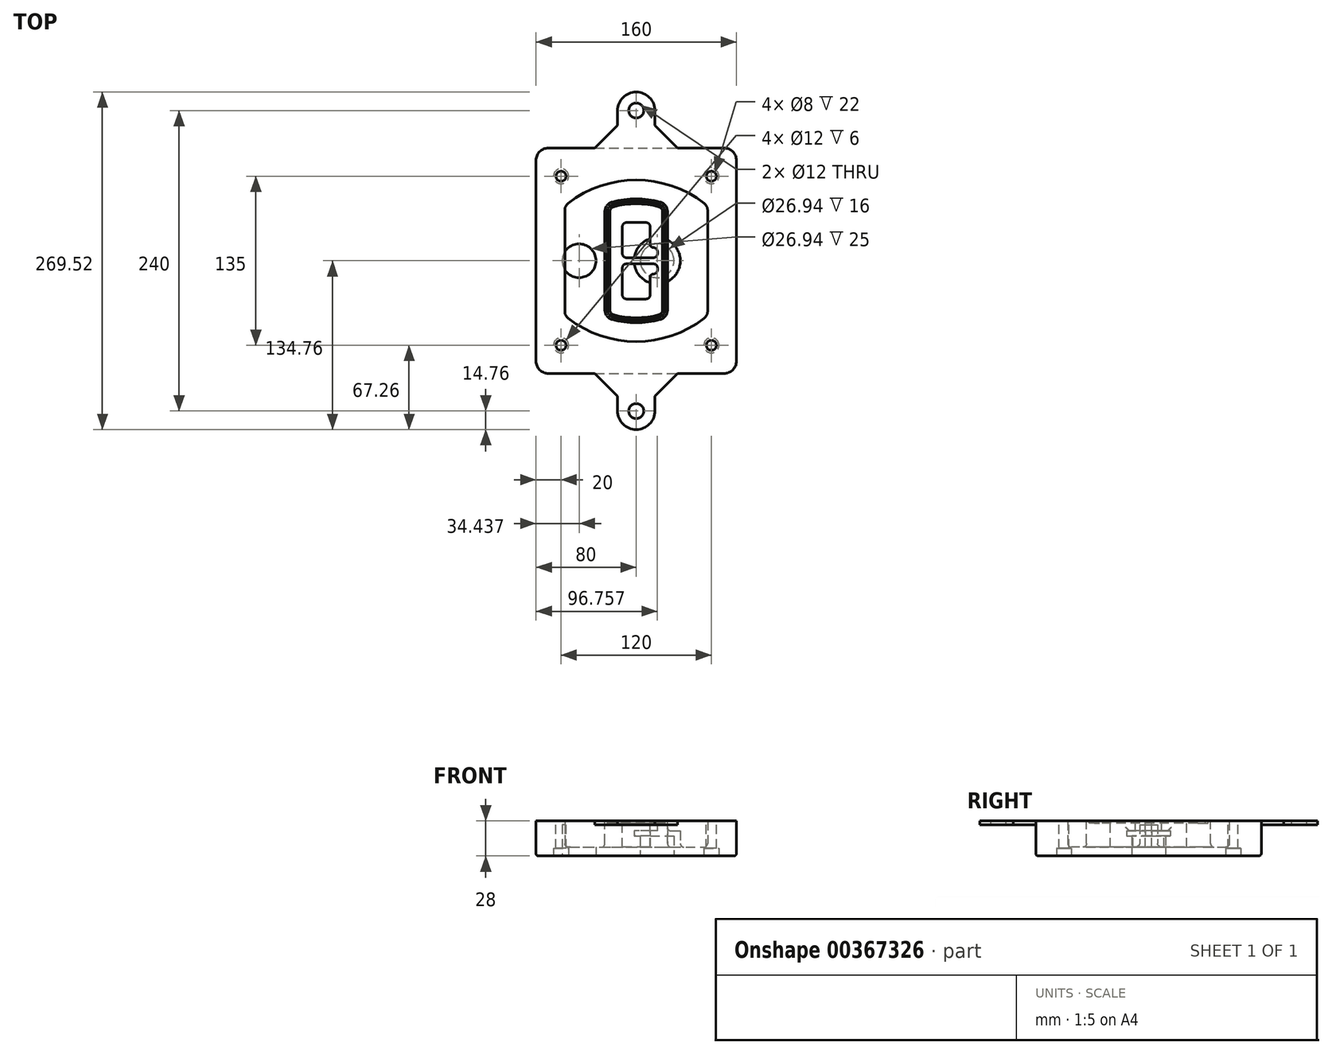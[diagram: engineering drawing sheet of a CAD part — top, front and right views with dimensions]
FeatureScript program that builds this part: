
annotation { "Feature Type Name" : "Feature", "Feature Type Description" : "" }
export const myFeature = defineFeature(function(context is Context, id is Id, definition is map)
    precondition{}
    {
        {
            var Q0;
            Q0=qCreatedBy(makeId("Top.planeOp"),FACE);
            var sketch = newSketch(context, id + "F0", { "sketchPlane" : qUnion([Q0])});
            skPoint(sketch, "E0.rect.middle", {"position": v(0, 0) * mm});
            skLineSegment(sketch, "E1.bottom", {"start": v(-70, -90) * mm, "end": v(70, -90) * mm});
            skLineSegment(sketch, "E1.top", {"start": v(-70, 90) * mm, "end": v(70, 90) * mm});
            skLineSegment(sketch, "E1.left", {"start": v(-80, -80) * mm, "end": v(-80, 80) * mm});
            skLineSegment(sketch, "E1.right", {"start": v(80, -80) * mm, "end": v(80, 80) * mm});
            skLineSegment(sketch, "E2", {"start": v(-80, 90) * mm, "end": v(80, -90) * mm, "construction": true});
            skLineSegment(sketch, "E3", {"start": v(80, 90) * mm, "end": v(-80, -90) * mm, "construction": true});
            skCircle(sketch, "E4", {"center": v(-60, 67.5) * mm, "radius": 4 * mm});
            skCircle(sketch, "E5", {"center": v(60, 67.5) * mm, "radius": 4 * mm});
            skCircle(sketch, "E6", {"center": v(60, -67.5) * mm, "radius": 4 * mm});
            skCircle(sketch, "E7", {"center": v(-60, -67.5) * mm, "radius": 4 * mm});
            skLineSegment(sketch, "E8", {"start": v(-60, 67.5) * mm, "end": v(60, 67.5) * mm, "construction": true});
            skLineSegment(sketch, "E9", {"start": v(60, 67.5) * mm, "end": v(60, -67.5) * mm, "construction": true});
            skLineSegment(sketch, "E10", {"start": v(60, -67.5) * mm, "end": v(-60, -67.5) * mm, "construction": true});
            skLineSegment(sketch, "E11", {"start": v(-60, -67.5) * mm, "end": v(-60, 67.5) * mm, "construction": true});
            skLineSegment(sketch, "E12", {"start": v(-60, 40.3) * mm, "end": v(-60, -40.3) * mm});
            skLineSegment(sketch, "E13", {"start": v(60, 40.3) * mm, "end": v(60, -40.3) * mm});
            skArc(sketch, "E14", {"start": v(56.15, 48.18) * mm, "mid": v(0, 67.5) * mm, "end": v(-56.15, 48.18) * mm});
            skArc(sketch, "E15", {"start": v(-56.15, -48.18) * mm, "mid": v(0, -67.5) * mm, "end": v(56.15, -48.18) * mm});
            skLineSegment(sketch, "E16", {"start": v(-60, 0) * mm, "end": v(60, 0) * mm, "construction": true});
            skPoint(sketch, "E17.visualSharp", {"position": v(-60, -45) * mm});
            skArc(sketch, "E17.filletArc", {"start": v(-60, -40.3) * mm, "mid": v(-58.99, -44.68) * mm, "end": v(-56.15, -48.18) * mm});
            skPoint(sketch, "E18.visualSharp", {"position": v(-60, 45) * mm});
            skArc(sketch, "E18.filletArc", {"start": v(-56.15, 48.18) * mm, "mid": v(-58.99, 44.68) * mm, "end": v(-60, 40.3) * mm});
            skPoint(sketch, "E19.visualSharp", {"position": v(60, 45) * mm});
            skArc(sketch, "E19.filletArc", {"start": v(60, 40.3) * mm, "mid": v(58.99, 44.68) * mm, "end": v(56.15, 48.18) * mm});
            skPoint(sketch, "E20.visualSharp", {"position": v(60, -45) * mm});
            skArc(sketch, "E20.filletArc", {"start": v(56.15, -48.18) * mm, "mid": v(58.99, -44.68) * mm, "end": v(60, -40.3) * mm});
            skPoint(sketch, "E21.visualSharp", {"position": v(-80, 90) * mm});
            skArc(sketch, "E21.filletArc", {"start": v(-70, 90) * mm, "mid": v(-77.07, 87.07) * mm, "end": v(-80, 80) * mm});
            skPoint(sketch, "E22.visualSharp", {"position": v(80, 90) * mm});
            skArc(sketch, "E22.filletArc", {"start": v(80, 80) * mm, "mid": v(77.07, 87.07) * mm, "end": v(70, 90) * mm});
            skPoint(sketch, "E23.visualSharp", {"position": v(80, -90) * mm});
            skArc(sketch, "E23.filletArc", {"start": v(70, -90) * mm, "mid": v(77.07, -87.07) * mm, "end": v(80, -80) * mm});
            skPoint(sketch, "E24.visualSharp", {"position": v(-80, -90) * mm});
            skArc(sketch, "E24.filletArc", {"start": v(-80, -80) * mm, "mid": v(-77.07, -87.07) * mm, "end": v(-70, -90) * mm});
            skArc(sketch, "E25.0", {"start": v(57, 40.3) * mm, "mid": v(56.3, 43.36) * mm, "end": v(54.3, 45.81) * mm});
            skLineSegment(sketch, "E25.1", {"start": v(57, 40.3) * mm, "end": v(57, -40.3) * mm});
            skArc(sketch, "E25.2", {"start": v(54.3, -45.81) * mm, "mid": v(56.3, -43.36) * mm, "end": v(57, -40.3) * mm});
            skArc(sketch, "E25.3", {"start": v(-54.3, -45.81) * mm, "mid": v(0, -64.5) * mm, "end": v(54.3, -45.81) * mm});
            skArc(sketch, "E25.4", {"start": v(-57, -40.3) * mm, "mid": v(-56.3, -43.36) * mm, "end": v(-54.3, -45.81) * mm});
            skArc(sketch, "E25.5", {"start": v(54.3, 45.81) * mm, "mid": v(0, 64.5) * mm, "end": v(-54.3, 45.81) * mm});
            skLineSegment(sketch, "E25.6", {"start": v(-57, 40.3) * mm, "end": v(-57, -40.3) * mm});
            skArc(sketch, "E25.7", {"start": v(-54.3, 45.81) * mm, "mid": v(-56.3, 43.36) * mm, "end": v(-57, 40.3) * mm});
            skArc(sketch, "E26.0", {"start": v(-58.62, 51.33) * mm, "mid": v(-62.58, 46.43) * mm, "end": v(-64, 40.3) * mm});
            skArc(sketch, "E26.1", {"start": v(58.62, 51.33) * mm, "mid": v(0, 71.5) * mm, "end": v(-58.62, 51.33) * mm});
            skArc(sketch, "E26.2", {"start": v(64, 40.3) * mm, "mid": v(62.58, 46.43) * mm, "end": v(58.62, 51.33) * mm});
            skLineSegment(sketch, "E26.3", {"start": v(64, 40.3) * mm, "end": v(64, -40.3) * mm});
            skArc(sketch, "E26.4", {"start": v(58.62, -51.33) * mm, "mid": v(62.58, -46.43) * mm, "end": v(64, -40.3) * mm});
            skLineSegment(sketch, "E26.5", {"start": v(-64, 40.3) * mm, "end": v(-64, -40.3) * mm});
            skArc(sketch, "E26.6", {"start": v(-58.62, -51.33) * mm, "mid": v(0, -71.5) * mm, "end": v(58.62, -51.33) * mm});
            skArc(sketch, "E26.7", {"start": v(-64, -40.3) * mm, "mid": v(-62.58, -46.43) * mm, "end": v(-58.62, -51.33) * mm});
            skSolve(sketch);
        }
        {
            var Q0;
            Q0=makeQuery(id+"F0.imprint","IMPRINT",FACE,{"disambiguationData":[TD([[makeQuery(id+"F0.imprint","IMPRINT",EDGE,{"derivedFrom":sQuery(id+"F0.wireOp",EDGE,"E1.bottom")}),1.0]])]});
            var Q1;
            Q1=makeQuery(id+"F0.imprint","IMPRINT",FACE,{"disambiguationData":[TD([[makeQuery(id+"F0.imprint","IMPRINT",EDGE,{"derivedFrom":sQuery(id+"F0.wireOp",EDGE,"E12")}),1.0]])]});
            var Q2;
            Q2=makeQuery(id+"F0.imprint","IMPRINT",FACE,{"disambiguationData":[TD([[makeQuery(id+"F0.imprint","IMPRINT",EDGE,{"derivedFrom":sQuery(id+"F0.wireOp",EDGE,"E25.0")}),1.0]])]});
            var Q3;
            Q3=makeQuery(id+"F0.imprint","IMPRINT",FACE,{"disambiguationData":[TD([[makeQuery(id+"F0.imprint","IMPRINT",EDGE,{"derivedFrom":sQuery(id+"F0.wireOp",EDGE,"E12")}),-1.0]])]});
            extrude(context, id + "F1", {"entities" : qUnion([Q0, Q1, Q2, Q3]), "oppositeDirection" : true, "depth" : 25 * mm});
        }
        {
            var Q0;
            Q0=makeQuery(id+"F0.imprint","IMPRINT",FACE,{"disambiguationData":[TD([[makeQuery(id+"F0.imprint","IMPRINT",EDGE,{"derivedFrom":sQuery(id+"F0.wireOp",EDGE,"E12")}),1.0]])]});
            extrude(context, id + "F2", {"entities" : qUnion([Q0]), "operationType" : NewBodyOperationType.ADD, "depth" : 3 * mm});
        }
        {
            var Q0;
            Q0=makeQuery(id+"F0.imprint","IMPRINT",FACE,{"disambiguationData":[TD([[makeQuery(id+"F0.imprint","IMPRINT",EDGE,{"derivedFrom":sQuery(id+"F0.wireOp",EDGE,"E25.0")}),1.0]])]});
            extrude(context, id + "F3", {"entities" : qUnion([Q0]), "operationType" : NewBodyOperationType.REMOVE, "oppositeDirection" : true, "depth" : 18 * mm});
        }
        {
            var Q0;
            Q0=makeQuery(id+"F2.opExtrude","CAP_FACE",FACE,{"disambiguationData":[OSD([sQuery(id+"F0.wireOp",EDGE,"E12"),sQuery(id+"F0.wireOp",EDGE,"E13"),sQuery(id+"F0.wireOp",EDGE,"E14"),sQuery(id+"F0.wireOp",EDGE,"E15"),sQuery(id+"F0.wireOp",EDGE,"E17.filletArc"),sQuery(id+"F0.wireOp",EDGE,"E18.filletArc"),sQuery(id+"F0.wireOp",EDGE,"E19.filletArc"),sQuery(id+"F0.wireOp",EDGE,"E20.filletArc"),sQuery(id+"F0.wireOp",EDGE,"E25.0"),sQuery(id+"F0.wireOp",EDGE,"E25.1"),sQuery(id+"F0.wireOp",EDGE,"E25.2"),sQuery(id+"F0.wireOp",EDGE,"E25.3"),sQuery(id+"F0.wireOp",EDGE,"E25.4"),sQuery(id+"F0.wireOp",EDGE,"E25.5"),sQuery(id+"F0.wireOp",EDGE,"E25.6"),sQuery(id+"F0.wireOp",EDGE,"E25.7")])],"isStart":false});
            var sketch = newSketch(context, id + "F4", { "sketchPlane" : qUnion([Q0])});
            skArc(sketch, "E27.0", {"start": v(-19.08, -46.97) * mm, "mid": v(0, -49.5) * mm, "end": v(19.08, -46.97) * mm});
            skArc(sketch, "E28.0", {"start": v(19.08, 46.97) * mm, "mid": v(0, 49.5) * mm, "end": v(-19.08, 46.97) * mm});
            skLineSegment(sketch, "E29", {"start": v(-25, 39.25) * mm, "end": v(-25, -39.25) * mm});
            skLineSegment(sketch, "E30", {"start": v(25, 39.25) * mm, "end": v(25, -39.25) * mm});
            skLineSegment(sketch, "E31", {"start": v(-25, 45.1) * mm, "end": v(25, 45.1) * mm, "construction": true});
            skLineSegment(sketch, "E32", {"start": v(-25, -45.1) * mm, "end": v(25, -45.1) * mm, "construction": true});
            skPoint(sketch, "E33.visualSharp", {"position": v(-25, 45.1) * mm});
            skArc(sketch, "E33.filletArc", {"start": v(-19.08, 46.97) * mm, "mid": v(-23.35, 44.11) * mm, "end": v(-25, 39.25) * mm});
            skPoint(sketch, "E34.visualSharp", {"position": v(25, 45.1) * mm});
            skArc(sketch, "E34.filletArc", {"start": v(25, 39.25) * mm, "mid": v(23.35, 44.11) * mm, "end": v(19.08, 46.97) * mm});
            skPoint(sketch, "E35.visualSharp", {"position": v(25, -45.1) * mm});
            skArc(sketch, "E35.filletArc", {"start": v(19.08, -46.97) * mm, "mid": v(23.35, -44.11) * mm, "end": v(25, -39.25) * mm});
            skPoint(sketch, "E36.visualSharp", {"position": v(-25, -45.1) * mm});
            skArc(sketch, "E36.filletArc", {"start": v(-25, -39.25) * mm, "mid": v(-23.35, -44.11) * mm, "end": v(-19.08, -46.97) * mm});
            skArc(sketch, "E37.0", {"start": v(54.3, 45.81) * mm, "mid": v(0, 64.5) * mm, "end": v(-54.3, 45.81) * mm});
            skArc(sketch, "E37.1", {"start": v(-54.3, 45.81) * mm, "mid": v(-56.3, 43.36) * mm, "end": v(-57, 40.3) * mm});
            skLineSegment(sketch, "E37.2", {"start": v(-57, 40.3) * mm, "end": v(-57, -40.3) * mm});
            skArc(sketch, "E37.3", {"start": v(-57, -40.3) * mm, "mid": v(-56.3, -43.36) * mm, "end": v(-54.3, -45.81) * mm});
            skArc(sketch, "E37.4", {"start": v(-54.3, -45.81) * mm, "mid": v(0, -64.5) * mm, "end": v(54.3, -45.81) * mm});
            skArc(sketch, "E37.5", {"start": v(54.3, -45.81) * mm, "mid": v(56.3, -43.36) * mm, "end": v(57, -40.3) * mm});
            skLineSegment(sketch, "E37.6", {"start": v(57, 40.3) * mm, "end": v(57, -40.3) * mm});
            skArc(sketch, "E37.7", {"start": v(57, 40.3) * mm, "mid": v(56.3, 43.36) * mm, "end": v(54.3, 45.81) * mm});
            skLineSegment(sketch, "E38.0", {"start": v(23, 39.25) * mm, "end": v(23, -39.25) * mm});
            skArc(sketch, "E38.1", {"start": v(18.56, -45.04) * mm, "mid": v(21.76, -42.9) * mm, "end": v(23, -39.25) * mm});
            skArc(sketch, "E38.2", {"start": v(-18.56, -45.04) * mm, "mid": v(0, -47.5) * mm, "end": v(18.56, -45.04) * mm});
            skArc(sketch, "E38.3", {"start": v(-23, -39.25) * mm, "mid": v(-21.76, -42.9) * mm, "end": v(-18.56, -45.04) * mm});
            skLineSegment(sketch, "E38.4", {"start": v(-23, 39.25) * mm, "end": v(-23, -39.25) * mm});
            skArc(sketch, "E38.5", {"start": v(23, 39.25) * mm, "mid": v(21.76, 42.9) * mm, "end": v(18.56, 45.04) * mm});
            skArc(sketch, "E38.6", {"start": v(-18.56, 45.04) * mm, "mid": v(-21.76, 42.9) * mm, "end": v(-23, 39.25) * mm});
            skArc(sketch, "E38.7", {"start": v(18.56, 45.04) * mm, "mid": v(0, 47.5) * mm, "end": v(-18.56, 45.04) * mm});
            skArc(sketch, "E39.0", {"start": v(21, 39.25) * mm, "mid": v(20.18, 41.68) * mm, "end": v(18.04, 43.1) * mm});
            skLineSegment(sketch, "E39.1", {"start": v(21, 39.25) * mm, "end": v(21, -39.25) * mm});
            skArc(sketch, "E39.2", {"start": v(18.04, -43.1) * mm, "mid": v(20.18, -41.68) * mm, "end": v(21, -39.25) * mm});
            skArc(sketch, "E39.3", {"start": v(-18.04, -43.1) * mm, "mid": v(0, -45.5) * mm, "end": v(18.04, -43.1) * mm});
            skArc(sketch, "E39.4", {"start": v(-21, -39.25) * mm, "mid": v(-20.18, -41.68) * mm, "end": v(-18.04, -43.1) * mm});
            skArc(sketch, "E39.5", {"start": v(18.04, 43.1) * mm, "mid": v(0, 45.5) * mm, "end": v(-18.04, 43.1) * mm});
            skLineSegment(sketch, "E39.6", {"start": v(-21, 39.25) * mm, "end": v(-21, -39.25) * mm});
            skArc(sketch, "E39.7", {"start": v(-18.04, 43.1) * mm, "mid": v(-20.18, 41.68) * mm, "end": v(-21, 39.25) * mm});
            skLineSegment(sketch, "E40", {"start": v(-25, 0) * mm, "end": v(25, 0) * mm, "construction": true});
            skLineSegment(sketch, "E41", {"start": v(-11, 5.5) * mm, "end": v(-11, 27.5) * mm});
            skLineSegment(sketch, "E42", {"start": v(-8, 30.5) * mm, "end": v(8, 30.5) * mm});
            skLineSegment(sketch, "E43", {"start": v(11, 27.5) * mm, "end": v(11, 13.5) * mm});
            skLineSegment(sketch, "E44", {"start": v(14, 10.5) * mm, "end": v(14, 10.5) * mm});
            skLineSegment(sketch, "E45", {"start": v(17, 7.5) * mm, "end": v(17, 5.5) * mm});
            skLineSegment(sketch, "E46", {"start": v(14, 2.5) * mm, "end": v(-8, 2.5) * mm});
            skPoint(sketch, "E47.visualSharp", {"position": v(-11, 30.5) * mm});
            skArc(sketch, "E47.filletArc", {"start": v(-8, 30.5) * mm, "mid": v(-10.12, 29.62) * mm, "end": v(-11, 27.5) * mm});
            skPoint(sketch, "E48.visualSharp", {"position": v(11, 30.5) * mm});
            skArc(sketch, "E48.filletArc", {"start": v(11, 27.5) * mm, "mid": v(10.12, 29.62) * mm, "end": v(8, 30.5) * mm});
            skPoint(sketch, "E49.visualSharp", {"position": v(11, 10.5) * mm});
            skArc(sketch, "E49.filletArc", {"start": v(11, 13.5) * mm, "mid": v(11.88, 11.38) * mm, "end": v(14, 10.5) * mm});
            skPoint(sketch, "E50.visualSharp", {"position": v(17, 10.5) * mm});
            skArc(sketch, "E50.filletArc", {"start": v(17, 7.5) * mm, "mid": v(16.12, 9.62) * mm, "end": v(14, 10.5) * mm});
            skPoint(sketch, "E51.visualSharp", {"position": v(17, 2.5) * mm});
            skArc(sketch, "E51.filletArc", {"start": v(14, 2.5) * mm, "mid": v(16.12, 3.38) * mm, "end": v(17, 5.5) * mm});
            skPoint(sketch, "E52.visualSharp", {"position": v(-11, 2.5) * mm});
            skArc(sketch, "E52.filletArc", {"start": v(-11, 5.5) * mm, "mid": v(-10.12, 3.38) * mm, "end": v(-8, 2.5) * mm});
            skLineSegment(sketch, "E53.0.MirrorCS", {"start": v(14, -2.5) * mm, "end": v(-8, -2.5) * mm});
            skArc(sketch, "E54.0.MirrorCS", {"start": v(-11, -5.5) * mm, "mid": v(-10.12, -3.38) * mm, "end": v(-8, -2.5) * mm});
            skLineSegment(sketch, "E55.0.MirrorCS", {"start": v(-11, -5.5) * mm, "end": v(-11, -27.5) * mm});
            skArc(sketch, "E56.0.MirrorCS", {"start": v(-8, -30.5) * mm, "mid": v(-10.12, -29.62) * mm, "end": v(-11, -27.5) * mm});
            skLineSegment(sketch, "E57.0.MirrorCS", {"start": v(-8, -30.5) * mm, "end": v(8, -30.5) * mm});
            skArc(sketch, "E58.0.MirrorCS", {"start": v(11, -27.5) * mm, "mid": v(10.12, -29.62) * mm, "end": v(8, -30.5) * mm});
            skLineSegment(sketch, "E59.0.MirrorCS", {"start": v(11, -27.5) * mm, "end": v(11, -13.5) * mm});
            skArc(sketch, "E60.0.MirrorCS", {"start": v(11, -13.5) * mm, "mid": v(11.88, -11.38) * mm, "end": v(14, -10.5) * mm});
            skArc(sketch, "E61.0.MirrorCS", {"start": v(17, -7.5) * mm, "mid": v(16.12, -9.62) * mm, "end": v(14, -10.5) * mm});
            skLineSegment(sketch, "E62.0.MirrorCS", {"start": v(17, -7.5) * mm, "end": v(17, -5.5) * mm});
            skArc(sketch, "E63.0.MirrorCS", {"start": v(14, -2.5) * mm, "mid": v(16.12, -3.38) * mm, "end": v(17, -5.5) * mm});
            skSolve(sketch);
        }
        {
            var Q0;
            Q0=makeQuery(id+"F4.imprint","IMPRINT",FACE,{"disambiguationData":[TD([[makeQuery(id+"F4.imprint","IMPRINT",EDGE,{"derivedFrom":sQuery(id+"F4.wireOp",EDGE,"E27.0")}),1.0]])]});
            var Q1;
            Q1=makeQuery(id+"F4.imprint","IMPRINT",FACE,{"disambiguationData":[TD([[makeQuery(id+"F4.imprint","IMPRINT",EDGE,{"derivedFrom":sQuery(id+"F4.wireOp",EDGE,"E38.0")}),-1.0]])]});
            var Q2;
            Q2=makeQuery(id+"F4.imprint","IMPRINT",FACE,{"disambiguationData":[TD([[makeQuery(id+"F4.imprint","IMPRINT",EDGE,{"derivedFrom":sQuery(id+"F4.wireOp",EDGE,"E39.0")}),1.0]])]});
            extrude(context, id + "F5", {"entities" : qUnion([Q0, Q1, Q2]), "operationType" : NewBodyOperationType.ADD, "endBound" : BoundingType.UP_TO_NEXT, "oppositeDirection" : true, "depth" : 25 * mm});
        }
        {
            var Q0;
            Q0=makeQuery(id+"F4.imprint","IMPRINT",FACE,{"disambiguationData":[TD([[makeQuery(id+"F4.imprint","IMPRINT",EDGE,{"derivedFrom":sQuery(id+"F4.wireOp",EDGE,"E38.0")}),-1.0]])]});
            extrude(context, id + "F6", {"entities" : qUnion([Q0]), "operationType" : NewBodyOperationType.REMOVE, "oppositeDirection" : true, "depth" : 2 * mm});
        }
        {
            var Q0;
            Q0=makeQuery(id+"F1.opExtrude","CAP_FACE",FACE,{"disambiguationData":[OSD([sQuery(id+"F0.wireOp",EDGE,"E1.bottom"),sQuery(id+"F0.wireOp",EDGE,"E1.top"),sQuery(id+"F0.wireOp",EDGE,"E1.left"),sQuery(id+"F0.wireOp",EDGE,"E1.right"),sQuery(id+"F0.wireOp",EDGE,"E4"),sQuery(id+"F0.wireOp",EDGE,"E5"),sQuery(id+"F0.wireOp",EDGE,"E6"),sQuery(id+"F0.wireOp",EDGE,"E7"),sQuery(id+"F0.wireOp",EDGE,"E21.filletArc"),sQuery(id+"F0.wireOp",EDGE,"E22.filletArc"),sQuery(id+"F0.wireOp",EDGE,"E23.filletArc"),sQuery(id+"F0.wireOp",EDGE,"E24.filletArc")])],"isStart":false});
            var sketch = newSketch(context, id + "F7", { "sketchPlane" : qUnion([Q0])});
            skCircle(sketch, "E64", {"center": v(16.76, 0) * mm, "radius": 13.47 * mm});
            skCircle(sketch, "E65", {"center": v(-45.56, 0) * mm, "radius": 13.47 * mm});
            skLineSegment(sketch, "E66", {"start": v(80, 0) * mm, "end": v(-80, 0) * mm});
            skCircle(sketch, "E67", {"center": v(16.76, 0) * mm, "radius": 18.47 * mm});
            skCircle(sketch, "E68", {"center": v(60, -67.5) * mm, "radius": 6 * mm});
            skCircle(sketch, "E69", {"center": v(-60, -67.5) * mm, "radius": 6 * mm});
            skCircle(sketch, "E70", {"center": v(-60, 67.5) * mm, "radius": 6 * mm});
            skCircle(sketch, "E71", {"center": v(60, 67.5) * mm, "radius": 6 * mm});
            skSolve(sketch);
        }
        {
            var Q0;
            {var subQ1=sQuery(id+"F7.wireOp",EDGE,"E66");var subQ4=sQuery(id+"F7.wireOp",EDGE,"E64");var subQ6=makeQuery(id+"F7.imprint","INTERSECT",VERTEX,{"disambiguationData":[OD(0.0)],"derivedFrom":[subQ4,subQ1]});Q0=makeQuery(id+"F7.imprint","IMPRINT",FACE,{"disambiguationData":[TD([[makeQuery(id+"F7.imprint","IMPRINT",EDGE,{"disambiguationData":[TD([[subQ6,-1.0]])],"derivedFrom":subQ4}),-1.0]])]});}
            var Q1;
            {var subQ0=sQuery(id+"F7.wireOp",EDGE,"E66");var subQ1=sQuery(id+"F7.wireOp",EDGE,"E64");var subQ3=makeQuery(id+"F7.imprint","INTERSECT",VERTEX,{"disambiguationData":[OD(0.0)],"derivedFrom":[subQ1,subQ0]});Q1=makeQuery(id+"F7.imprint","IMPRINT",FACE,{"disambiguationData":[TD([[makeQuery(id+"F7.imprint","IMPRINT",EDGE,{"disambiguationData":[TD([[subQ3,-1.0]])],"derivedFrom":subQ1}),1.0]])]});}
            var Q2;
            {var subQ0=sQuery(id+"F7.wireOp",EDGE,"E66");var subQ1=sQuery(id+"F7.wireOp",EDGE,"E64");var subQ3=makeQuery(id+"F7.imprint","INTERSECT",VERTEX,{"disambiguationData":[OD(0.0)],"derivedFrom":[subQ1,subQ0]});Q2=makeQuery(id+"F7.imprint","IMPRINT",FACE,{"disambiguationData":[TD([[makeQuery(id+"F7.imprint","IMPRINT",EDGE,{"disambiguationData":[TD([[subQ3,1.0]])],"derivedFrom":subQ1}),1.0]])]});}
            var Q3;
            {var subQ1=sQuery(id+"F7.wireOp",EDGE,"E66");var subQ4=sQuery(id+"F7.wireOp",EDGE,"E64");var subQ6=makeQuery(id+"F7.imprint","INTERSECT",VERTEX,{"disambiguationData":[OD(0.0)],"derivedFrom":[subQ4,subQ1]});Q3=makeQuery(id+"F7.imprint","IMPRINT",FACE,{"disambiguationData":[TD([[makeQuery(id+"F7.imprint","IMPRINT",EDGE,{"disambiguationData":[TD([[subQ6,1.0]])],"derivedFrom":subQ4}),-1.0]])]});}
            extrude(context, id + "F8", {"entities" : qUnion([Q0, Q1, Q2, Q3]), "operationType" : NewBodyOperationType.ADD, "oppositeDirection" : true, "depth" : 20 * mm});
        }
        {
            var Q0;
            {var subQ0=sQuery(id+"F7.wireOp",EDGE,"E66");var subQ1=sQuery(id+"F7.wireOp",EDGE,"E64");var subQ3=makeQuery(id+"F7.imprint","INTERSECT",VERTEX,{"disambiguationData":[OD(0.0)],"derivedFrom":[subQ1,subQ0]});Q0=makeQuery(id+"F7.imprint","IMPRINT",FACE,{"disambiguationData":[TD([[makeQuery(id+"F7.imprint","IMPRINT",EDGE,{"disambiguationData":[TD([[subQ3,-1.0]])],"derivedFrom":subQ1}),1.0]])]});}
            var Q1;
            {var subQ0=sQuery(id+"F7.wireOp",EDGE,"E66");var subQ1=sQuery(id+"F7.wireOp",EDGE,"E64");var subQ3=makeQuery(id+"F7.imprint","INTERSECT",VERTEX,{"disambiguationData":[OD(0.0)],"derivedFrom":[subQ1,subQ0]});Q1=makeQuery(id+"F7.imprint","IMPRINT",FACE,{"disambiguationData":[TD([[makeQuery(id+"F7.imprint","IMPRINT",EDGE,{"disambiguationData":[TD([[subQ3,1.0]])],"derivedFrom":subQ1}),1.0]])]});}
            extrude(context, id + "F9", {"entities" : qUnion([Q0, Q1]), "operationType" : NewBodyOperationType.REMOVE, "oppositeDirection" : true, "depth" : 16 * mm});
        }
        {
            var Q0;
            {var subQ0=sQuery(id+"F7.wireOp",EDGE,"E66");var subQ1=sQuery(id+"F7.wireOp",EDGE,"E65");var subQ3=makeQuery(id+"F7.imprint","INTERSECT",VERTEX,{"disambiguationData":[OD(0.0)],"derivedFrom":[subQ1,subQ0]});Q0=makeQuery(id+"F7.imprint","IMPRINT",FACE,{"disambiguationData":[TD([[makeQuery(id+"F7.imprint","IMPRINT",EDGE,{"disambiguationData":[TD([[subQ3,-1.0]])],"derivedFrom":subQ1}),1.0]])]});}
            var Q1;
            {var subQ0=sQuery(id+"F7.wireOp",EDGE,"E66");var subQ1=sQuery(id+"F7.wireOp",EDGE,"E65");var subQ3=makeQuery(id+"F7.imprint","INTERSECT",VERTEX,{"disambiguationData":[OD(0.0)],"derivedFrom":[subQ1,subQ0]});Q1=makeQuery(id+"F7.imprint","IMPRINT",FACE,{"disambiguationData":[TD([[makeQuery(id+"F7.imprint","IMPRINT",EDGE,{"disambiguationData":[TD([[subQ3,1.0]])],"derivedFrom":subQ1}),1.0]])]});}
            extrude(context, id + "F10", {"entities" : qUnion([Q0, Q1]), "operationType" : NewBodyOperationType.REMOVE, "oppositeDirection" : true, "depth" : 25 * mm});
        }
        {
            var Q0;
            Q0=makeQuery(id+"F7.imprint","IMPRINT",FACE,{"disambiguationData":[TD([[makeQuery(id+"F7.imprint","IMPRINT",EDGE,{"derivedFrom":sQuery(id+"F7.wireOp",EDGE,"E68")}),1.0]])]});
            var Q1;
            Q1=makeQuery(id+"F7.imprint","IMPRINT",FACE,{"disambiguationData":[TD([[makeQuery(id+"F7.imprint","IMPRINT",EDGE,{"derivedFrom":makeQuery(id+"F1.opExtrude","CAP_EDGE",EDGE,{"disambiguationData":[OSD([sQuery(id+"F0.wireOp",EDGE,"E5")])],"isStart":false})}),-1.0]])]});
            var Q2;
            Q2=makeQuery(id+"F7.imprint","IMPRINT",FACE,{"disambiguationData":[TD([[makeQuery(id+"F7.imprint","IMPRINT",EDGE,{"derivedFrom":sQuery(id+"F7.wireOp",EDGE,"E69")}),1.0]])]});
            var Q3;
            Q3=makeQuery(id+"F7.imprint","IMPRINT",FACE,{"disambiguationData":[TD([[makeQuery(id+"F7.imprint","IMPRINT",EDGE,{"derivedFrom":makeQuery(id+"F1.opExtrude","CAP_EDGE",EDGE,{"disambiguationData":[OSD([sQuery(id+"F0.wireOp",EDGE,"E4")])],"isStart":false})}),-1.0]])]});
            var Q4;
            Q4=makeQuery(id+"F7.imprint","IMPRINT",FACE,{"disambiguationData":[TD([[makeQuery(id+"F7.imprint","IMPRINT",EDGE,{"derivedFrom":sQuery(id+"F7.wireOp",EDGE,"E70")}),1.0]])]});
            var Q5;
            Q5=makeQuery(id+"F7.imprint","IMPRINT",FACE,{"disambiguationData":[TD([[makeQuery(id+"F7.imprint","IMPRINT",EDGE,{"derivedFrom":makeQuery(id+"F1.opExtrude","CAP_EDGE",EDGE,{"disambiguationData":[OSD([sQuery(id+"F0.wireOp",EDGE,"E7")])],"isStart":false})}),-1.0]])]});
            var Q6;
            Q6=makeQuery(id+"F7.imprint","IMPRINT",FACE,{"disambiguationData":[TD([[makeQuery(id+"F7.imprint","IMPRINT",EDGE,{"derivedFrom":sQuery(id+"F7.wireOp",EDGE,"E71")}),1.0]])]});
            var Q7;
            Q7=makeQuery(id+"F7.imprint","IMPRINT",FACE,{"disambiguationData":[TD([[makeQuery(id+"F7.imprint","IMPRINT",EDGE,{"derivedFrom":makeQuery(id+"F1.opExtrude","CAP_EDGE",EDGE,{"disambiguationData":[OSD([sQuery(id+"F0.wireOp",EDGE,"E6")])],"isStart":false})}),-1.0]])]});
            extrude(context, id + "F11", {"entities" : qUnion([Q0, Q1, Q2, Q3, Q4, Q5, Q6, Q7]), "operationType" : NewBodyOperationType.REMOVE, "oppositeDirection" : true, "depth" : 6 * mm});
        }
        {
            var Q0;
            Q0=makeQuery(id+"F9.boolean.opBoolean","COPY",FACE,{"derivedFrom":makeQuery(id+"F9.opExtrude","CAP_FACE",FACE,{"disambiguationData":[OSD([sQuery(id+"F7.wireOp",EDGE,"E64")])],"isStart":false})});
            var sketch = newSketch(context, id + "F12", { "sketchPlane" : qUnion([Q0])});
            skArc(sketch, "E72.0", {"start": v(11, 17.55) * mm, "mid": v(2.57, 11.82) * mm, "end": v(-1.54, 2.5) * mm});
            skArc(sketch, "E72.1", {"start": v(-1.54, -2.5) * mm, "mid": v(2.57, -11.82) * mm, "end": v(11, -17.55) * mm});
            skLineSegment(sketch, "E73", {"start": v(-1.54, -2.5) * mm, "end": v(14, -2.5) * mm});
            skLineSegment(sketch, "E74.0", {"start": v(14, 2.5) * mm, "end": v(-1.54, 2.5) * mm});
            skArc(sketch, "E74.1", {"start": v(14, 2.5) * mm, "mid": v(16.12, 3.38) * mm, "end": v(17, 5.5) * mm});
            skLineSegment(sketch, "E74.2", {"start": v(17, 7.5) * mm, "end": v(17, 5.5) * mm});
            skArc(sketch, "E74.3", {"start": v(17, 7.5) * mm, "mid": v(16.12, 9.62) * mm, "end": v(14, 10.5) * mm});
            skArc(sketch, "E74.4", {"start": v(11, 13.5) * mm, "mid": v(11.88, 11.38) * mm, "end": v(14, 10.5) * mm});
            skLineSegment(sketch, "E74.5", {"start": v(11, 17.55) * mm, "end": v(11, 13.5) * mm});
            skLineSegment(sketch, "E74.7", {"start": v(14, -2.5) * mm, "end": v(-1.54, -2.5) * mm});
            skArc(sketch, "E74.8", {"start": v(14, -2.5) * mm, "mid": v(16.12, -3.38) * mm, "end": v(17, -5.5) * mm});
            skLineSegment(sketch, "E74.9", {"start": v(17, -7.5) * mm, "end": v(17, -5.5) * mm});
            skArc(sketch, "E74.10", {"start": v(17, -7.5) * mm, "mid": v(16.12, -9.62) * mm, "end": v(14, -10.5) * mm});
            skArc(sketch, "E74.11", {"start": v(11, -13.5) * mm, "mid": v(11.88, -11.38) * mm, "end": v(14, -10.5) * mm});
            skLineSegment(sketch, "E74.12", {"start": v(11, -17.55) * mm, "end": v(11, -13.5) * mm});
            skPoint(sketch, "E75.orphan", {"position": v(11, -27.5) * mm});
            skPoint(sketch, "E76.orphan", {"position": v(-8, -2.5) * mm});
            skPoint(sketch, "E77.orphan", {"position": v(-8, 2.5) * mm});
            skPoint(sketch, "E78.orphan", {"position": v(11, 27.5) * mm});
            skSolve(sketch);
        }
        {
            var Q0;
            {var subQ7=sQuery(id+"F12.wireOp",EDGE,"E72.0");var subQ14=sQuery(id+"F12.wireOp",EDGE,"E72.1");var subQ16=sQuery(id+"F12.wireOp",EDGE,"E74.1");var subQ18=sQuery(id+"F12.wireOp",EDGE,"E74.8");Q0=qUnion([makeQuery(id+"F12.imprint","IMPRINT",FACE,{"disambiguationData":[TD([[makeQuery(id+"F12.imprint","IMPRINT",EDGE,{"derivedFrom":subQ7}),1.0]])]}),makeQuery(id+"F12.imprint","IMPRINT",FACE,{"disambiguationData":[TD([[makeQuery(id+"F12.imprint","IMPRINT",EDGE,{"derivedFrom":subQ14}),1.0]])]}),makeQuery(id+"F12.imprint","IMPRINT",FACE,{"disambiguationData":[TD([[makeQuery(id+"F12.imprint","IMPRINT",EDGE,{"derivedFrom":subQ16}),1.0]])]}),makeQuery(id+"F12.imprint","IMPRINT",FACE,{"disambiguationData":[TD([[makeQuery(id+"F12.imprint","IMPRINT",EDGE,{"derivedFrom":subQ18}),-1.0]])]})]);}
            var Q1;
            Q1=makeQuery(id+"F5.boolean.opBoolean","SPLIT",FACE,{"disambiguationData":[TD([makeQuery(id+"F5.opExtrude","SWEPT_FACE",FACE,{"disambiguationData":[OSD([sQuery(id+"F4.wireOp",EDGE,"E41")])]})])],"derivedFrom":makeQuery(id+"F3.boolean.opBoolean","COPY",FACE,{"derivedFrom":makeQuery(id+"F3.opExtrude","CAP_FACE",FACE,{"disambiguationData":[OSD([sQuery(id+"F0.wireOp",EDGE,"E25.0"),sQuery(id+"F0.wireOp",EDGE,"E25.1"),sQuery(id+"F0.wireOp",EDGE,"E25.2"),sQuery(id+"F0.wireOp",EDGE,"E25.3"),sQuery(id+"F0.wireOp",EDGE,"E25.4"),sQuery(id+"F0.wireOp",EDGE,"E25.5"),sQuery(id+"F0.wireOp",EDGE,"E25.6"),sQuery(id+"F0.wireOp",EDGE,"E25.7")])],"isStart":false})})});
            extrude(context, id + "F13", {"entities" : qUnion([Q0]), "operationType" : NewBodyOperationType.REMOVE, "endBound" : BoundingType.UP_TO_SURFACE, "endBoundEntityFace" : qUnion([Q1]), "depth" : 25 * mm});
        }
        {
            var Q0;
            Q0=makeQuery(id+"F3.boolean.opBoolean","COPY",EDGE,{"derivedFrom":makeQuery(id+"F3.opExtrude","CAP_EDGE",EDGE,{"disambiguationData":[OSD([sQuery(id+"F0.wireOp",EDGE,"E25.6")])],"isStart":false})});
            var Q1;
            Q1=makeQuery(id+"F8.boolean.opBoolean","INTERSECT",EDGE,{"derivedFrom":[makeQuery(id+"F5.opExtrude","SWEPT_FACE",FACE,{"disambiguationData":[OSD([sQuery(id+"F4.wireOp",EDGE,"E30")])]}),makeQuery(id+"F8.opExtrude","CAP_FACE",FACE,{"disambiguationData":[OSD([sQuery(id+"F7.wireOp",EDGE,"E67")])],"isStart":false})]});
            var Q2;
            Q2=makeQuery(id+"F8.boolean.opBoolean","INTERSECT",EDGE,{"disambiguationData":[OD(1.0)],"derivedFrom":[makeQuery(id+"F5.opExtrude","SWEPT_FACE",FACE,{"disambiguationData":[OSD([sQuery(id+"F4.wireOp",EDGE,"E30")])]}),makeQuery(id+"F8.opExtrude","SWEPT_FACE",FACE,{"disambiguationData":[OSD([sQuery(id+"F7.wireOp",EDGE,"E67")])]})]});
            var Q3;
            {var subQ0=sQuery(id+"F4.wireOp",EDGE,"E30");Q3=makeQuery(id+"F8.boolean.opBoolean","SPLIT",EDGE,{"disambiguationData":[TD([makeQuery(id+"F5.opExtrude","SWEPT_FACE",FACE,{"disambiguationData":[OSD([sQuery(id+"F4.wireOp",EDGE,"E35.filletArc")])]})])],"derivedFrom":makeQuery(id+"F5.opExtrude","CAP_EDGE",EDGE,{"disambiguationData":[OSD([subQ0])],"isStart":false})});}
            var Q4;
            {var subQ0=sQuery(id+"F0.wireOp",EDGE,"E25.7");var subQ1=sQuery(id+"F0.wireOp",EDGE,"E25.1");var subQ2=sQuery(id+"F0.wireOp",EDGE,"E25.6");var subQ3=sQuery(id+"F0.wireOp",EDGE,"E25.5");var subQ4=sQuery(id+"F0.wireOp",EDGE,"E25.4");var subQ5=sQuery(id+"F0.wireOp",EDGE,"E25.0");var subQ6=sQuery(id+"F0.wireOp",EDGE,"E25.2");var subQ7=sQuery(id+"F0.wireOp",EDGE,"E25.3");Q4=makeQuery(id+"F8.boolean.opBoolean","INTERSECT",EDGE,{"derivedFrom":[makeQuery(id+"F5.boolean.opBoolean","SPLIT",FACE,{"disambiguationData":[TD([makeQuery(id+"F2.opExtrude","SWEPT_FACE",FACE,{"disambiguationData":[OSD([subQ5])]})])],"derivedFrom":makeQuery(id+"F3.boolean.opBoolean","COPY",FACE,{"derivedFrom":makeQuery(id+"F3.opExtrude","CAP_FACE",FACE,{"disambiguationData":[OSD([subQ5,subQ1,subQ6,subQ7,subQ4,subQ3,subQ2,subQ0])],"isStart":false})})}),makeQuery(id+"F8.opExtrude","SWEPT_FACE",FACE,{"disambiguationData":[OSD([sQuery(id+"F7.wireOp",EDGE,"E67")])]})]});}
            var Q5;
            Q5=makeQuery(id+"F8.boolean.opBoolean","INTERSECT",EDGE,{"disambiguationData":[OD(0.0)],"derivedFrom":[makeQuery(id+"F5.opExtrude","SWEPT_FACE",FACE,{"disambiguationData":[OSD([sQuery(id+"F4.wireOp",EDGE,"E30")])]}),makeQuery(id+"F8.opExtrude","SWEPT_FACE",FACE,{"disambiguationData":[OSD([sQuery(id+"F7.wireOp",EDGE,"E67")])]})]});
            fillet(context, id + "F14", {"entities" : qUnion([Q0, Q1, Q2, Q3, Q4, Q5]), "radius" : 3 * mm, "tangentPropagation" : true, "allowEdgeOverflow" : false});
        }
        {
            var Q0;
            Q0=makeQuery(id+"F1.opExtrude","CAP_EDGE",EDGE,{"disambiguationData":[OSD([sQuery(id+"F0.wireOp",EDGE,"E1.bottom")])],"isStart":false});
            fillet(context, id + "F15", {"entities" : qUnion([Q0]), "radius" : 2 * mm, "tangentPropagation" : true, "allowEdgeOverflow" : false});
        }
        {
            var Q0;
            {var subQ0=sQuery(id+"F0.wireOp",EDGE,"E21.filletArc");var subQ1=sQuery(id+"F0.wireOp",EDGE,"E7");var subQ2=sQuery(id+"F0.wireOp",EDGE,"E6");var subQ3=sQuery(id+"F0.wireOp",EDGE,"E5");var subQ4=sQuery(id+"F0.wireOp",EDGE,"E4");var subQ5=sQuery(id+"F0.wireOp",EDGE,"E22.filletArc");var subQ6=sQuery(id+"F0.wireOp",EDGE,"E1.bottom");var subQ7=sQuery(id+"F0.wireOp",EDGE,"E1.right");var subQ8=sQuery(id+"F0.wireOp",EDGE,"E1.top");var subQ9=sQuery(id+"F0.wireOp",EDGE,"E1.left");var subQ10=sQuery(id+"F0.wireOp",EDGE,"E23.filletArc");var subQ11=sQuery(id+"F0.wireOp",EDGE,"E24.filletArc");Q0=makeQuery(id+"F2.boolean.opBoolean","SPLIT",FACE,{"disambiguationData":[TD([makeQuery(id+"F1.opExtrude","SWEPT_FACE",FACE,{"disambiguationData":[OSD([subQ6])]})])],"derivedFrom":makeQuery(id+"F1.opExtrude","CAP_FACE",FACE,{"disambiguationData":[OSD([subQ6,subQ8,subQ9,subQ7,subQ4,subQ3,subQ2,subQ1,subQ0,subQ5,subQ10,subQ11])],"isStart":true})});}
            var sketch = newSketch(context, id + "F16", { "sketchPlane" : qUnion([Q0])});
            skLineSegment(sketch, "E79", {"start": v(0, 90) * mm, "end": v(0, 120) * mm, "construction": true});
            skPoint(sketch, "E79.endSnap0", {"position": v(0, 90) * mm});
            skCircle(sketch, "E80", {"center": v(0, 120) * mm, "radius": 6 * mm});
            skLineSegment(sketch, "E81", {"start": v(-15, 108) * mm, "end": v(-33, 90) * mm});
            skLineSegment(sketch, "E82", {"start": v(-15, 108) * mm, "end": v(-15, 119.76) * mm});
            skLineSegment(sketch, "E83.MirrorCS", {"start": v(15, 108) * mm, "end": v(15, 119.76) * mm});
            skLineSegment(sketch, "E84.MirrorCS", {"start": v(15, 108) * mm, "end": v(33, 90) * mm});
            skArc(sketch, "E85", {"start": v(15, 119.76) * mm, "mid": v(0, 134.76) * mm, "end": v(-15, 119.76) * mm});
            skLineSegment(sketch, "E86", {"start": v(-105.2, 0) * mm, "end": v(106.15, 0) * mm, "construction": true});
            skLineSegment(sketch, "E87.MirrorCS", {"start": v(-15, -108) * mm, "end": v(-33, -90) * mm});
            skLineSegment(sketch, "E88.MirrorCS", {"start": v(15, -108) * mm, "end": v(33, -90) * mm});
            skLineSegment(sketch, "E89.MirrorCS", {"start": v(-15, -108) * mm, "end": v(-15, -119.76) * mm});
            skLineSegment(sketch, "E90.MirrorCS", {"start": v(15, -108) * mm, "end": v(15, -119.76) * mm});
            skArc(sketch, "E91.MirrorCS", {"start": v(15, -119.76) * mm, "mid": v(0, -134.76) * mm, "end": v(-15, -119.76) * mm});
            skCircle(sketch, "E92.MirrorC", {"center": v(0, -120) * mm, "radius": 6 * mm});
            skLineSegment(sketch, "E93.MirrorCS", {"start": v(0, -90) * mm, "end": v(0, -120) * mm, "construction": true});
            skSolve(sketch);
        }
        {
            var Q0;
            Q0=makeQuery(id+"F16.imprint","IMPRINT",FACE,{"disambiguationData":[TD([[makeQuery(id+"F16.imprint","IMPRINT",EDGE,{"derivedFrom":sQuery(id+"F16.wireOp",EDGE,"E80")}),-1.0]])]});
            var Q1;
            {var subQ1=sQuery(id+"F16.wireOp",EDGE,"E87.MirrorCS");Q1=makeQuery(id+"F16.imprint","IMPRINT",FACE,{"disambiguationData":[TD([[makeQuery(id+"F16.imprint","IMPRINT",EDGE,{"derivedFrom":subQ1}),-1.0]])]});}
            var Q2;
            Q2=makeQuery(id+"F16.imprint","IMPRINT",FACE,{"disambiguationData":[TD([[makeQuery(id+"F16.imprint","IMPRINT",EDGE,{"derivedFrom":makeQuery(id+"F1.opExtrude","CAP_EDGE",EDGE,{"disambiguationData":[OSD([sQuery(id+"F0.wireOp",EDGE,"E1.left")])],"isStart":true})}),-1.0]])]});
            var Q3;
            Q3=makeQuery(id+"F2.opExtrude","CAP_FACE",FACE,{"disambiguationData":[OSD([sQuery(id+"F0.wireOp",EDGE,"E12"),sQuery(id+"F0.wireOp",EDGE,"E13"),sQuery(id+"F0.wireOp",EDGE,"E14"),sQuery(id+"F0.wireOp",EDGE,"E15"),sQuery(id+"F0.wireOp",EDGE,"E17.filletArc"),sQuery(id+"F0.wireOp",EDGE,"E18.filletArc"),sQuery(id+"F0.wireOp",EDGE,"E19.filletArc"),sQuery(id+"F0.wireOp",EDGE,"E20.filletArc"),sQuery(id+"F0.wireOp",EDGE,"E25.0"),sQuery(id+"F0.wireOp",EDGE,"E25.1"),sQuery(id+"F0.wireOp",EDGE,"E25.2"),sQuery(id+"F0.wireOp",EDGE,"E25.3"),sQuery(id+"F0.wireOp",EDGE,"E25.4"),sQuery(id+"F0.wireOp",EDGE,"E25.5"),sQuery(id+"F0.wireOp",EDGE,"E25.6"),sQuery(id+"F0.wireOp",EDGE,"E25.7")])],"isStart":false});
            extrude(context, id + "F17", {"entities" : qUnion([Q0, Q1, Q2]), "operationType" : NewBodyOperationType.ADD, "endBound" : BoundingType.UP_TO_SURFACE, "endBoundEntityFace" : qUnion([Q3]), "depth" : 25 * mm});
        }
    });
